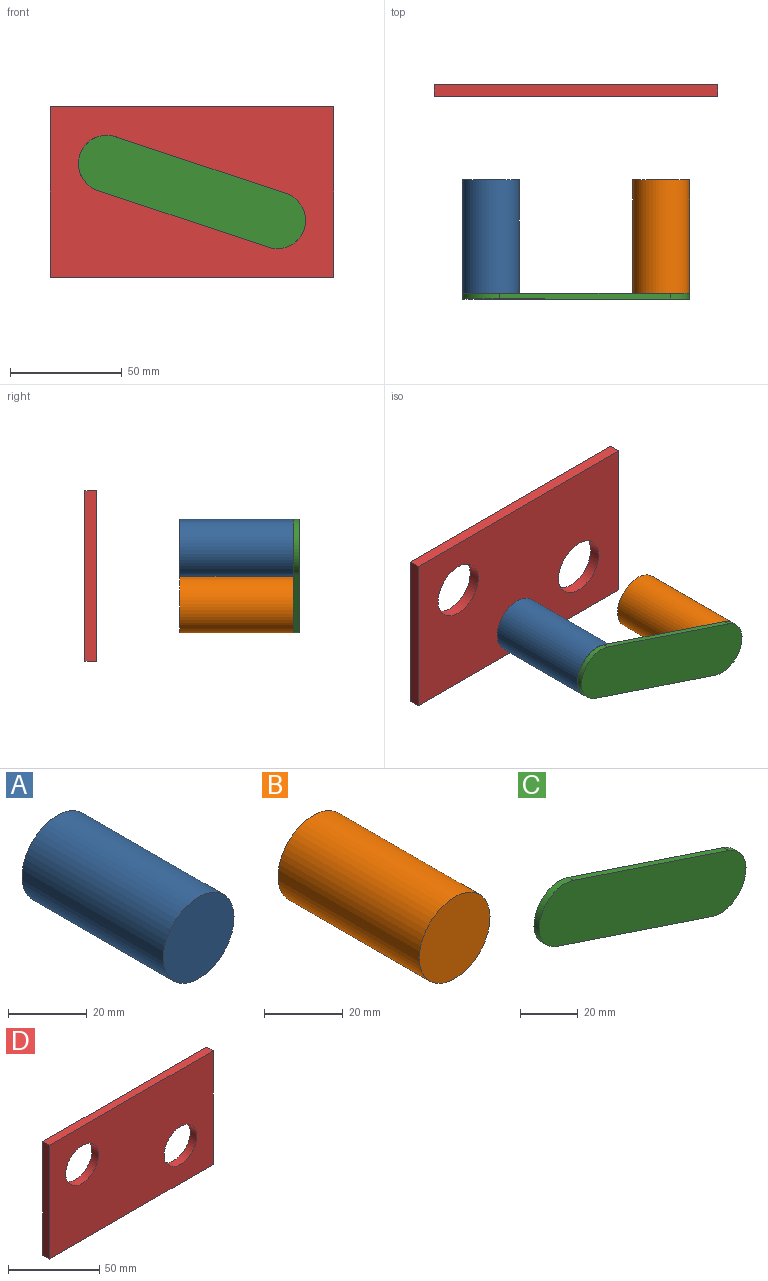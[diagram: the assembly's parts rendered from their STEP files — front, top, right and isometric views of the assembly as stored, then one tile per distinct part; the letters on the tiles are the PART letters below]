
ASSEMBLY  parts=4 mates=5
PART A: 3 faces, bbox 25.4x50.8x25.4 mm
  f0: cylinder r=12.7mm len=50.8mm, axis (0,1,0), area 4053.7mm2, adj f1,f2
  f1: plane 25.4x25.4mm, normal (0,-1,0), area 506.7mm2, adj f0
  f2: plane 25.4x25.4mm, normal (0,1,0), area 506.7mm2, adj f0
PART B: 3 faces, bbox 25.4x50.8x25.4 mm
  f0: cylinder r=12.7mm len=50.8mm, axis (0,1,0), area 4053.7mm2, adj f1,f2
  f1: plane 25.4x25.4mm, normal (0,-1,0), area 506.7mm2, adj f0
  f2: plane 25.4x25.4mm, normal (0,1,0), area 506.7mm2, adj f0
PART C: 6 faces, bbox 101.6x2.5x50.8 mm
  f0: plane 76.2x25.4mm, normal (0.32,0,0.95), area 204mm2, adj f1,f3,f4,f5
  f1: cylinder r=12.7mm len=24.75mm, axis (0,1,0), area 101.3mm2, adj f0,f2,f4,f5
  f2: plane 76.2x25.4mm, normal (-0.32,0,-0.95), area 204mm2, adj f1,f3,f4,f5
  f3: cylinder r=12.7mm len=24.75mm, axis (0,1,0), area 101.3mm2, adj f0,f2,f4,f5
  f4: plane 101.6x50.8mm, normal (0,-1,0), area 2546.9mm2, adj f0,f1,f2,f3
  f5: plane 101.6x50.8mm, normal (0,1,0), area 2546.9mm2, adj f0,f1,f2,f3
PART D: 8 faces, bbox 127x5.1x76.2 mm
  f0: plane 127x5.08mm, normal (0,0,1), area 645.2mm2, adj f1,f5,f6,f7
  f1: plane 76.2x5.08mm, normal (-1,0,0), area 387.1mm2, adj f0,f2,f6,f7
  f2: plane 127x5.08mm, normal (0,0,-1), area 645.2mm2, adj f1,f5,f6,f7
  f3: cylinder r=12.7mm len=25.4mm, axis (0,1,0), area 405.4mm2, adj f6,f7
  f4: cylinder r=12.7mm len=25.4mm, axis (0,1,0), area 405.4mm2, adj f6,f7
  f5: plane 76.2x5.08mm, normal (1,0,0), area 387.1mm2, adj f0,f2,f6,f7
  f6: plane 127x76.2mm, normal (0,-1,0), area 8664mm2, adj f0,f1,f2,f3,f4,f5
  f7: plane 127x76.2mm, normal (0,1,0), area 8664mm2, adj f0,f1,f2,f3,f4,f5
PLACE A t=(8.98,-38.02,-4.94)mm
PLACE B t=(8.98,-38.02,-4.94)mm
PLACE C t=(8.98,-38.02,-4.94)mm
PLACE D t=(8.98,4.43,-4.94)mm fixed
MATE slider C.f3 <-> B.f0  axis (0,1,0) through (47.08,-90.09,-17.64)mm
MATE fastened B.f0 <-> C.f3  axis (0,-1,0) through (47.08,-88.82,-17.64)mm
MATE fastened A.f0 <-> C.f1  axis (0,-1,0) through (-29.12,-88.82,7.76)mm
MATE slider A.f0 <-> D.f3  axis (0,1,0) through (-29.12,-63.42,7.76)mm
MATE slider B.f0 <-> D.f4  axis (0,1,0) through (47.08,-38.02,-17.64)mm
